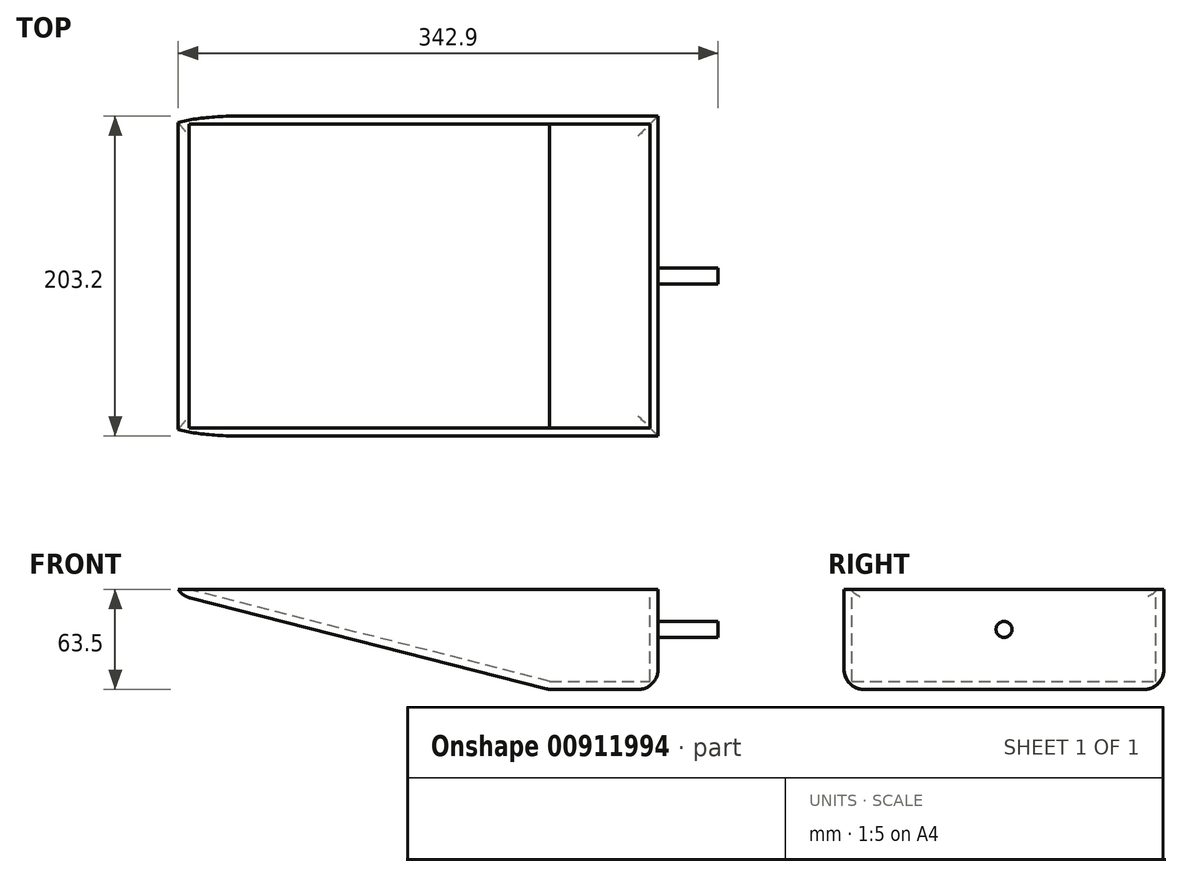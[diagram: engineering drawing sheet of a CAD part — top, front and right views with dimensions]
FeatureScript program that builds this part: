
annotation { "Feature Type Name" : "Feature", "Feature Type Description" : "" }
export const myFeature = defineFeature(function(context is Context, id is Id, definition is map)
    precondition{}
    {
        {
            var Q0;
            Q0=qCreatedBy(makeId("Front.planeOp"),FACE);
            var sketch = newSketch(context, id + "F0", { "sketchPlane" : qUnion([Q0])});
            skLineSegment(sketch, "E0.bottom", {"start": v(-154.98, -14.95) * mm, "end": v(161.41, -14.95) * mm});
            skLineSegment(sketch, "E0.left", {"start": v(-154.98, -14.95) * mm, "end": v(-154.98, -14.95) * mm});
            skLineSegment(sketch, "E0.right", {"start": v(149.82, -0.11) * mm, "end": v(149.82, -70.22) * mm});
            skPoint(sketch, "E1.visualSharp", {"position": v(-154.98, -18.4) * mm});
            skLineSegment(sketch, "E2", {"start": v(80.32, -78.45) * mm, "end": v(146.08, -78.45) * mm});
            skLineSegment(sketch, "E3", {"start": v(-153.1, -18.88) * mm, "end": v(80.32, -78.45) * mm});
            skLineSegment(sketch, "E4", {"start": v(-154.98, -14.95) * mm, "end": v(-154.98, -16.39) * mm});
            skPoint(sketch, "E5.visualSharp", {"position": v(149.82, -14.95) * mm});
            skLineSegment(sketch, "E6", {"start": v(-153.1, -18.88) * mm, "end": v(-154.98, -18.4) * mm});
            skLineSegment(sketch, "E7", {"start": v(-154.98, -16.39) * mm, "end": v(-154.98, -18.4) * mm});
            skLineSegment(sketch, "E8", {"start": v(146.08, -78.45) * mm, "end": v(149.82, -78.45) * mm});
            skLineSegment(sketch, "E9", {"start": v(149.82, -78.45) * mm, "end": v(149.82, -70.22) * mm});
            skSolve(sketch);
        }
        {
            var Q0;
            Q0=makeQuery(id+"F0.imprint","IMPRINT",FACE,{"disambiguationData":[TD([[makeQuery(id+"F0.imprint","IMPRINT",EDGE,{"derivedFrom":sQuery(id+"F0.wireOp",EDGE,"E0.bottom")}),-1.0]])]});
            extrude(context, id + "F1", {"entities" : qUnion([Q0]), "depth" : 203.2 * mm, "offsetDistance" : 25.4 * mm});
        }
        {
            var Q0;
            Q0=makeQuery(id+"F1.opExtrude","SWEPT_FACE",FACE,{"disambiguationData":[OSD([sQuery(id+"F0.wireOp",EDGE,"E0.bottom")])]});
            shell(context, id + "F2", {"entities" : qUnion([Q0]), "thickness" : 5.08 * mm});
        }
        {
            var Q0;
            Q0=makeQuery(id+"F1.opExtrude","SWEPT_FACE",FACE,{"disambiguationData":[OSD([sQuery(id+"F0.wireOp",EDGE,"E0.right")])]});
            var sketch = newSketch(context, id + "F3", { "sketchPlane" : qUnion([Q0])});
            skCircle(sketch, "E10", {"center": v(-101.6, -40.35) * mm, "radius": 5.08 * mm});
            skSolve(sketch);
        }
        {
            var Q0;
            Q0 = qSketchRegion(id + "F3", true);
            extrude(context, id + "F4", {"entities" : qUnion([Q0]), "operationType" : NewBodyOperationType.ADD, "depth" : 38.1 * mm, "offsetDistance" : 25.4 * mm});
        }
        {
            var Q0;
            Q0=makeQuery(id+"F1.opExtrude","SWEPT_FACE",FACE,{"disambiguationData":[OSD([sQuery(id+"F0.wireOp",EDGE,"E2"),sQuery(id+"F0.wireOp",EDGE,"E3")])]});
            fillet(context, id + "F5", {"entities" : qUnion([Q0]), "radius" : 12.7 * mm, "tangentPropagation" : true, "allowEdgeOverflow" : false});
        }
    });
